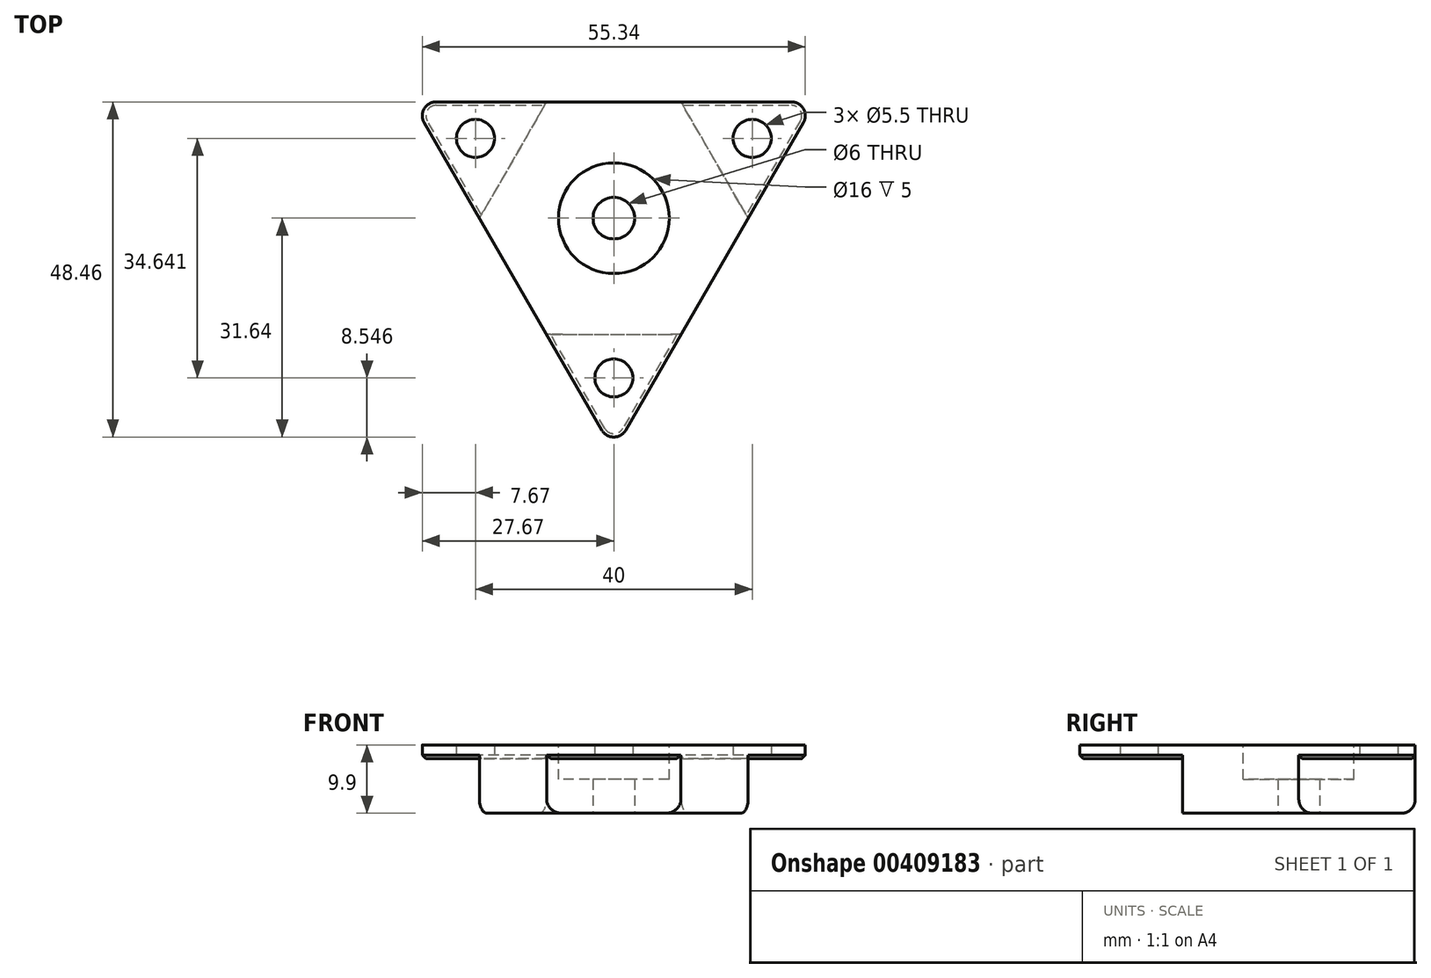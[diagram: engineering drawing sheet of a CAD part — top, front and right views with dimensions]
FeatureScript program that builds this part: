
annotation { "Feature Type Name" : "Feature", "Feature Type Description" : "" }
export const myFeature = defineFeature(function(context is Context, id is Id, definition is map)
    precondition{}
    {
        {
            var Q0;
            Q0=qCreatedBy(makeId("Top.planeOp"),FACE);
            var sketch = newSketch(context, id + "F0", { "sketchPlane" : qUnion([Q0])});
            skLineSegment(sketch, "E0", {"start": v(-30, 17.32) * mm, "end": v(30, 17.32) * mm, "construction": true});
            skLineSegment(sketch, "E1", {"start": v(30, 17.32) * mm, "end": v(0, -34.64) * mm, "construction": true});
            skLineSegment(sketch, "E2", {"start": v(0, -34.64) * mm, "end": v(-30, 17.32) * mm, "construction": true});
            skCircle(sketch, "E3", {"center": v(0, 0) * mm, "radius": 34.64 * mm, "construction": true});
            skCircle(sketch, "E4", {"center": v(-20, 11.55) * mm, "radius": 2.75 * mm});
            skLineSegment(sketch, "E5", {"start": v(-10, 17.32) * mm, "end": v(-20, 0) * mm, "construction": true});
            skLineSegment(sketch, "E6", {"start": v(-15, 8.66) * mm, "end": v(0, 0) * mm, "construction": true});
            skPoint(sketch, "E7.center", {"position": v(-45.27, -13.55) * mm});
            skCircle(sketch, "E8", {"center": v(-20, 11.55) * mm, "radius": 5.77 * mm, "construction": true});
            skCircle(sketch, "E9", {"center": v(0, 0) * mm, "radius": 10 * mm, "construction": true});
            skCircle(sketch, "E10", {"center": v(0, 0) * mm, "radius": 3 * mm});
            skLineSegment(sketch, "E11.0", {"start": v(0, -33.64) * mm, "end": v(-29.13, 16.82) * mm});
            skLineSegment(sketch, "E11.1", {"start": v(29.13, 16.82) * mm, "end": v(0, -33.64) * mm});
            skLineSegment(sketch, "E11.2", {"start": v(-29.13, 16.82) * mm, "end": v(29.13, 16.82) * mm});
            skLineSegment(sketch, "E12.0", {"start": v(-9.71, 16.82) * mm, "end": v(-19.42, 0) * mm});
            skCircle(sketch, "E13.1.0", {"center": v(0, -23.1) * mm, "radius": 2.75 * mm});
            skLineSegment(sketch, "E13.1.1", {"start": v(-9.71, -16.82) * mm, "end": v(9.71, -16.82) * mm});
            skCircle(sketch, "E13.2.0", {"center": v(20, 11.55) * mm, "radius": 2.75 * mm});
            skLineSegment(sketch, "E13.2.1", {"start": v(19.42, 0) * mm, "end": v(9.71, 16.82) * mm});
            skSolve(sketch);
        }
        {
            var Q0;
            Q0 = qSketchRegion(id + "F0", true);
            extrude(context, id + "F1", {"entities" : qUnion([Q0]), "depth" : 9.9 * mm});
        }
        {
            var Q0;
            Q0=makeQuery(id+"F0.imprint","IMPRINT",FACE,{"disambiguationData":[TD([[makeQuery(id+"F0.imprint","IMPRINT",EDGE,{"derivedFrom":sQuery(id+"F0.wireOp",EDGE,"E13.2.0")}),-1.0]])]});
            var Q1;
            Q1=makeQuery(id+"F0.imprint","IMPRINT",FACE,{"disambiguationData":[TD([[makeQuery(id+"F0.imprint","IMPRINT",EDGE,{"derivedFrom":sQuery(id+"F0.wireOp",EDGE,"E13.1.0")}),-1.0]])]});
            var Q2;
            Q2=makeQuery(id+"F0.imprint","IMPRINT",FACE,{"disambiguationData":[TD([[makeQuery(id+"F0.imprint","IMPRINT",EDGE,{"derivedFrom":sQuery(id+"F0.wireOp",EDGE,"E4")}),-1.0]])]});
            extrude(context, id + "F2", {"entities" : qUnion([Q0, Q1, Q2]), "operationType" : NewBodyOperationType.REMOVE, "depth" : 7.9 * mm});
        }
        {
            var Q0;
            Q0=makeQuery(id+"F1.opExtrude","CAP_FACE",FACE,{"disambiguationData":[OSD([sQuery(id+"F0.wireOp",EDGE,"E0"),sQuery(id+"F0.wireOp",EDGE,"E1"),sQuery(id+"F0.wireOp",EDGE,"E2"),sQuery(id+"F0.wireOp",EDGE,"E4"),sQuery(id+"F0.wireOp",EDGE,"3f91073c-f4cf-4afd-b99c-0fb4fe4cd3df.1.0"),sQuery(id+"F0.wireOp",EDGE,"3f91073c-f4cf-4afd-b99c-0fb4fe4cd3df.2.0"),sQuery(id+"F0.wireOp",EDGE,"E10")])],"isStart":false});
            var sketch = newSketch(context, id + "F3", { "sketchPlane" : qUnion([Q0])});
            skCircle(sketch, "E14", {"center": v(0, 0) * mm, "radius": 8 * mm});
            skSolve(sketch);
        }
        {
            var Q0;
            Q0=makeQuery(id+"F3.imprint","IMPRINT",FACE,{"disambiguationData":[TD([[makeQuery(id+"F3.imprint","IMPRINT",EDGE,{"derivedFrom":sQuery(id+"F3.wireOp",EDGE,"E14")}),1.0]])]});
            extrude(context, id + "F4", {"entities" : qUnion([Q0]), "operationType" : NewBodyOperationType.REMOVE, "oppositeDirection" : true, "depth" : 5 * mm});
        }
        {
            var Q0;
            Q0=makeQuery(id+"F1.opExtrude","SWEPT_EDGE",EDGE,{"disambiguationData":[OSD([sQuery(id+"F0.wireOp",EDGE,"E11.0"),sQuery(id+"F0.wireOp",EDGE,"E11.2")])]});
            var Q1;
            Q1=makeQuery(id+"F2.boolean.opBoolean","COPY",EDGE,{"derivedFrom":makeQuery(id+"F2.opExtrude","SWEPT_EDGE",EDGE,{"disambiguationData":[OSD([sQuery(id+"F0.wireOp",EDGE,"E11.2"),sQuery(id+"F0.wireOp",EDGE,"E12.0")])]})});
            var Q2;
            Q2=makeQuery(id+"F2.boolean.opBoolean","COPY",EDGE,{"derivedFrom":makeQuery(id+"F2.opExtrude","SWEPT_EDGE",EDGE,{"disambiguationData":[OSD([sQuery(id+"F0.wireOp",EDGE,"E11.0"),sQuery(id+"F0.wireOp",EDGE,"E12.0")])]})});
            var Q3;
            Q3=makeQuery(id+"F2.boolean.opBoolean","COPY",EDGE,{"derivedFrom":makeQuery(id+"F2.opExtrude","SWEPT_EDGE",EDGE,{"disambiguationData":[OSD([sQuery(id+"F0.wireOp",EDGE,"E11.2"),sQuery(id+"F0.wireOp",EDGE,"E13.2.1")])]})});
            var Q4;
            Q4=makeQuery(id+"F2.boolean.opBoolean","COPY",EDGE,{"derivedFrom":makeQuery(id+"F2.opExtrude","CAP_EDGE",EDGE,{"disambiguationData":[OSD([sQuery(id+"F0.wireOp",EDGE,"E13.2.1")])],"isStart":true})});
            var Q5;
            Q5=makeQuery(id+"F1.opExtrude","CAP_EDGE",EDGE,{"disambiguationData":[OSD([sQuery(id+"F0.wireOp",EDGE,"E11.2")])],"isStart":true});
            var Q6;
            Q6=makeQuery(id+"F2.boolean.opBoolean","COPY",EDGE,{"derivedFrom":makeQuery(id+"F2.opExtrude","CAP_EDGE",EDGE,{"disambiguationData":[OSD([sQuery(id+"F0.wireOp",EDGE,"E12.0")])],"isStart":true})});
            var Q7;
            Q7=makeQuery(id+"F1.opExtrude","CAP_EDGE",EDGE,{"disambiguationData":[OSD([sQuery(id+"F0.wireOp",EDGE,"E11.0")])],"isStart":true});
            var Q8;
            Q8=makeQuery(id+"F2.boolean.opBoolean","COPY",EDGE,{"derivedFrom":makeQuery(id+"F2.opExtrude","CAP_EDGE",EDGE,{"disambiguationData":[OSD([sQuery(id+"F0.wireOp",EDGE,"E13.1.1")])],"isStart":true})});
            var Q9;
            Q9=makeQuery(id+"F2.boolean.opBoolean","COPY",EDGE,{"derivedFrom":makeQuery(id+"F2.opExtrude","SWEPT_EDGE",EDGE,{"disambiguationData":[OSD([sQuery(id+"F0.wireOp",EDGE,"E11.1"),sQuery(id+"F0.wireOp",EDGE,"E13.2.1")])]})});
            var Q10;
            Q10=makeQuery(id+"F2.boolean.opBoolean","COPY",EDGE,{"derivedFrom":makeQuery(id+"F2.opExtrude","SWEPT_EDGE",EDGE,{"disambiguationData":[OSD([sQuery(id+"F0.wireOp",EDGE,"E11.1"),sQuery(id+"F0.wireOp",EDGE,"E13.1.1")])]})});
            var Q11;
            Q11=makeQuery(id+"F1.opExtrude","SWEPT_EDGE",EDGE,{"disambiguationData":[OSD([sQuery(id+"F0.wireOp",EDGE,"E11.0"),sQuery(id+"F0.wireOp",EDGE,"E11.1")])]});
            var Q12;
            Q12=makeQuery(id+"F1.opExtrude","SWEPT_EDGE",EDGE,{"disambiguationData":[OSD([sQuery(id+"F0.wireOp",EDGE,"E11.1"),sQuery(id+"F0.wireOp",EDGE,"E11.2")])]});
            var Q13;
            Q13=makeQuery(id+"F2.boolean.opBoolean","COPY",EDGE,{"derivedFrom":makeQuery(id+"F2.opExtrude","SWEPT_EDGE",EDGE,{"disambiguationData":[OSD([sQuery(id+"F0.wireOp",EDGE,"E11.0"),sQuery(id+"F0.wireOp",EDGE,"E13.1.1")])]})});
            var Q14;
            Q14=makeQuery(id+"F1.opExtrude","CAP_EDGE",EDGE,{"disambiguationData":[OSD([sQuery(id+"F0.wireOp",EDGE,"E11.1")])],"isStart":true});
            fillet(context, id + "F5", {"entities" : qUnion([Q0, Q1, Q2, Q3, Q4, Q5, Q6, Q7, Q8, Q9, Q10, Q11, Q12, Q13, Q14]), "radius" : 2 * mm, "tangentPropagation" : true, "allowEdgeOverflow" : false});
        }
        {
            var Q0;
            {var subQ0=sQuery(id+"F0.wireOp",EDGE,"E11.1");var subQ1=sQuery(id+"F0.wireOp",EDGE,"E11.0");Q0=makeQuery(id+"F5.opFillet","BLEND_EDGE",EDGE,{"blendedFrom":[makeQuery(id+"F1.opExtrude","SWEPT_EDGE",EDGE,{"disambiguationData":[OSD([subQ1,subQ0])]}),makeQuery(id+"F2.boolean.opBoolean","COPY",FACE,{"derivedFrom":makeQuery(id+"F2.opExtrude","CAP_FACE",FACE,{"disambiguationData":[OSD([subQ1,subQ0,sQuery(id+"F0.wireOp",EDGE,"E13.1.0"),sQuery(id+"F0.wireOp",EDGE,"E13.1.1")])],"isStart":false})})],"blendedInto":[makeQuery(id+"F2.boolean.opBoolean","COPY",FACE,{"derivedFrom":makeQuery(id+"F2.opExtrude","CAP_FACE",FACE,{"disambiguationData":[OSD([subQ1,subQ0,sQuery(id+"F0.wireOp",EDGE,"E13.1.0"),sQuery(id+"F0.wireOp",EDGE,"E13.1.1")])],"isStart":false})})]});}
            var Q1;
            {var subQ0=sQuery(id+"F0.wireOp",EDGE,"E11.2");var subQ1=sQuery(id+"F0.wireOp",EDGE,"E11.0");Q1=makeQuery(id+"F5.opFillet","BLEND_EDGE",EDGE,{"blendedFrom":[makeQuery(id+"F1.opExtrude","SWEPT_EDGE",EDGE,{"disambiguationData":[OSD([subQ1,subQ0])]}),makeQuery(id+"F2.boolean.opBoolean","COPY",FACE,{"derivedFrom":makeQuery(id+"F2.opExtrude","CAP_FACE",FACE,{"disambiguationData":[OSD([sQuery(id+"F0.wireOp",EDGE,"E4"),subQ1,subQ0,sQuery(id+"F0.wireOp",EDGE,"E12.0")])],"isStart":false})})],"blendedInto":[makeQuery(id+"F2.boolean.opBoolean","COPY",FACE,{"derivedFrom":makeQuery(id+"F2.opExtrude","CAP_FACE",FACE,{"disambiguationData":[OSD([sQuery(id+"F0.wireOp",EDGE,"E4"),subQ1,subQ0,sQuery(id+"F0.wireOp",EDGE,"E12.0")])],"isStart":false})})]});}
            var Q2;
            {var subQ0=sQuery(id+"F0.wireOp",EDGE,"E11.2");var subQ1=sQuery(id+"F0.wireOp",EDGE,"E11.1");Q2=makeQuery(id+"F5.opFillet","BLEND_EDGE",EDGE,{"blendedFrom":[makeQuery(id+"F1.opExtrude","SWEPT_EDGE",EDGE,{"disambiguationData":[OSD([subQ1,subQ0])]}),makeQuery(id+"F2.boolean.opBoolean","COPY",FACE,{"derivedFrom":makeQuery(id+"F2.opExtrude","CAP_FACE",FACE,{"disambiguationData":[OSD([subQ1,subQ0,sQuery(id+"F0.wireOp",EDGE,"E13.2.0"),sQuery(id+"F0.wireOp",EDGE,"E13.2.1")])],"isStart":false})})],"blendedInto":[makeQuery(id+"F2.boolean.opBoolean","COPY",FACE,{"derivedFrom":makeQuery(id+"F2.opExtrude","CAP_FACE",FACE,{"disambiguationData":[OSD([subQ1,subQ0,sQuery(id+"F0.wireOp",EDGE,"E13.2.0"),sQuery(id+"F0.wireOp",EDGE,"E13.2.1")])],"isStart":false})})]});}
            chamfer(context, id + "F6", {"entities" : qUnion([Q0, Q1, Q2]), "width" : 0.5 * mm, "tangentPropagation" : true});
        }
    });
